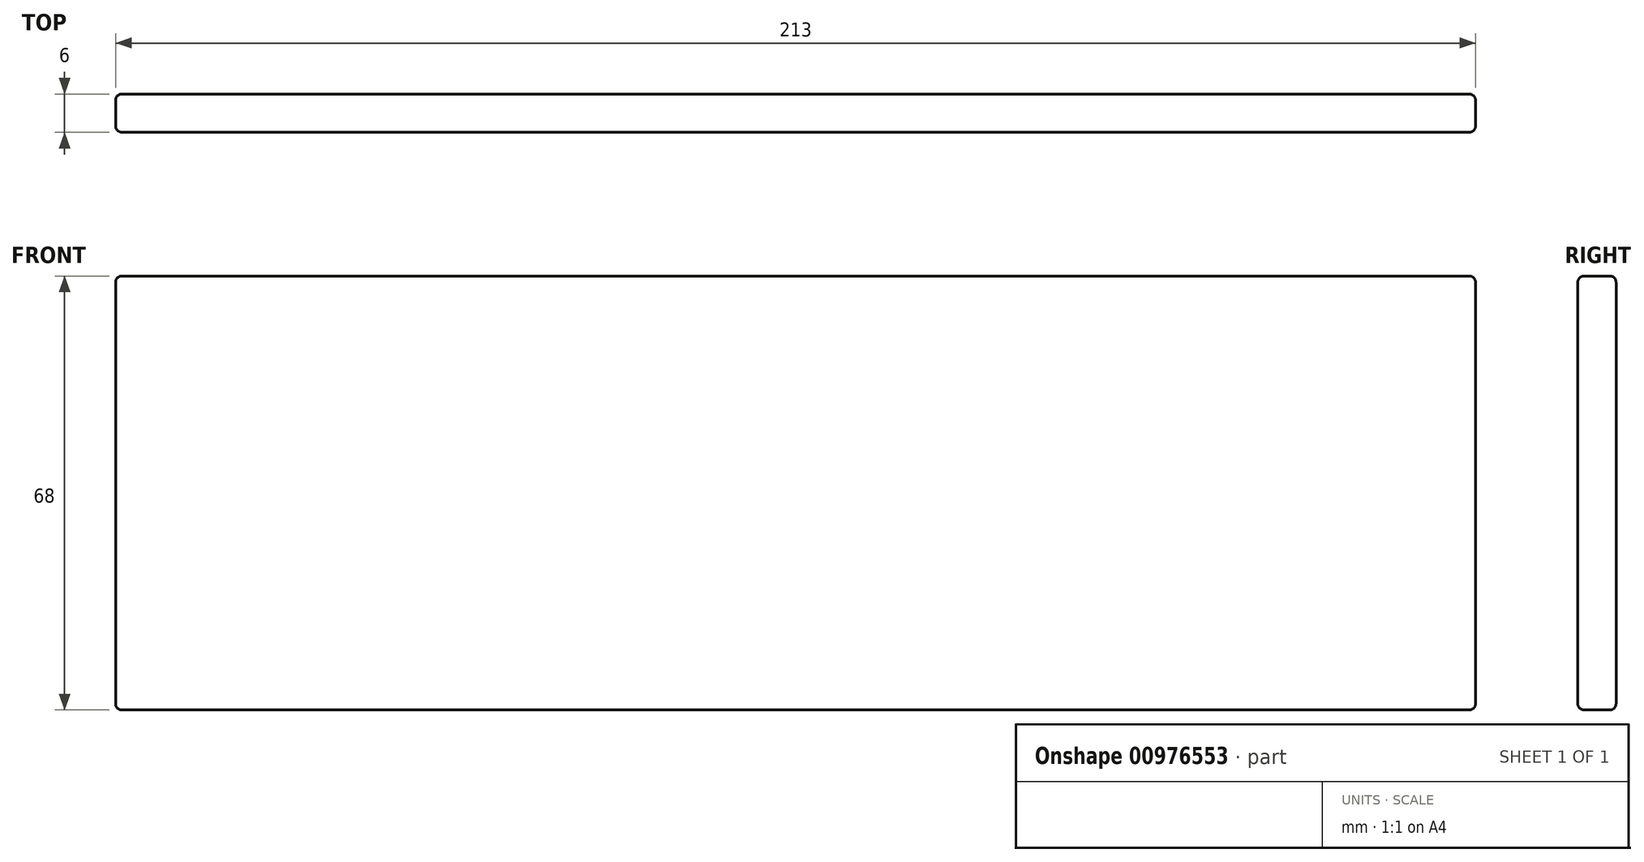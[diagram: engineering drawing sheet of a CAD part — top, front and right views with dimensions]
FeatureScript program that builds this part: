
annotation { "Feature Type Name" : "Feature", "Feature Type Description" : "" }
export const myFeature = defineFeature(function(context is Context, id is Id, definition is map)
    precondition{}
    {
        {
            var Q0;
            Q0=qCreatedBy(makeId("Front.planeOp"),FACE);
            var sketch = newSketch(context, id + "F0", { "sketchPlane" : qUnion([Q0])});
            skLineSegment(sketch, "E0.bottom", {"start": v(-106.5, 0) * mm, "end": v(106.5, 0) * mm});
            skLineSegment(sketch, "E0.top", {"start": v(-106.5, -68) * mm, "end": v(106.5, -68) * mm});
            skLineSegment(sketch, "E0.left", {"start": v(-106.5, 0) * mm, "end": v(-106.5, -68) * mm});
            skLineSegment(sketch, "E0.right", {"start": v(106.5, 0) * mm, "end": v(106.5, -68) * mm});
            skSolve(sketch);
        }
        {
            var Q0;
            Q0=makeQuery(id+"F0.imprint","IMPRINT",FACE,{"disambiguationData":[TD([[makeQuery(id+"F0.imprint","IMPRINT",EDGE,{"derivedFrom":sQuery(id+"F0.wireOp",EDGE,"E0.bottom")}),-1.0]])]});
            extrude(context, id + "F1", {"entities" : qUnion([Q0]), "endBound" : BoundingType.SYMMETRIC, "depth" : 6 * mm, "offsetDistance" : 25 * mm});
        }
        {
            var Q0;
            Q0=makeQuery(id+"F1.opExtrude","CAP_FACE",FACE,{"disambiguationData":[OSD([sQuery(id+"F0.wireOp",EDGE,"E0.bottom"),sQuery(id+"F0.wireOp",EDGE,"E0.top"),sQuery(id+"F0.wireOp",EDGE,"E0.left"),sQuery(id+"F0.wireOp",EDGE,"E0.right")])],"isStart":false});
            var Q1;
            Q1=makeQuery(id+"F1.opExtrude","CAP_FACE",FACE,{"disambiguationData":[OSD([sQuery(id+"F0.wireOp",EDGE,"E0.bottom"),sQuery(id+"F0.wireOp",EDGE,"E0.top"),sQuery(id+"F0.wireOp",EDGE,"E0.left"),sQuery(id+"F0.wireOp",EDGE,"E0.right")])],"isStart":true});
            var Q2;
            Q2=makeQuery(id+"F1.opExtrude","SWEPT_EDGE",EDGE,{"disambiguationData":[OSD([sQuery(id+"F0.wireOp",EDGE,"E0.bottom"),sQuery(id+"F0.wireOp",EDGE,"E0.left")])]});
            var Q3;
            Q3=makeQuery(id+"F1.opExtrude","SWEPT_EDGE",EDGE,{"disambiguationData":[OSD([sQuery(id+"F0.wireOp",EDGE,"E0.bottom"),sQuery(id+"F0.wireOp",EDGE,"E0.right")])]});
            var Q4;
            Q4=makeQuery(id+"F1.opExtrude","SWEPT_EDGE",EDGE,{"disambiguationData":[OSD([sQuery(id+"F0.wireOp",EDGE,"E0.top"),sQuery(id+"F0.wireOp",EDGE,"E0.right")])]});
            var Q5;
            Q5=makeQuery(id+"F1.opExtrude","SWEPT_EDGE",EDGE,{"disambiguationData":[OSD([sQuery(id+"F0.wireOp",EDGE,"E0.top"),sQuery(id+"F0.wireOp",EDGE,"E0.left")])]});
            fillet(context, id + "F2", {"entities" : qUnion([Q0, Q1, Q2, Q3, Q4, Q5]), "tangentPropagation" : true, "radius" : 1 * mm, "defaultsChanged" : true, "vertexSettings" : [], "allowEdgeOverflow" : false});
        }
    });
